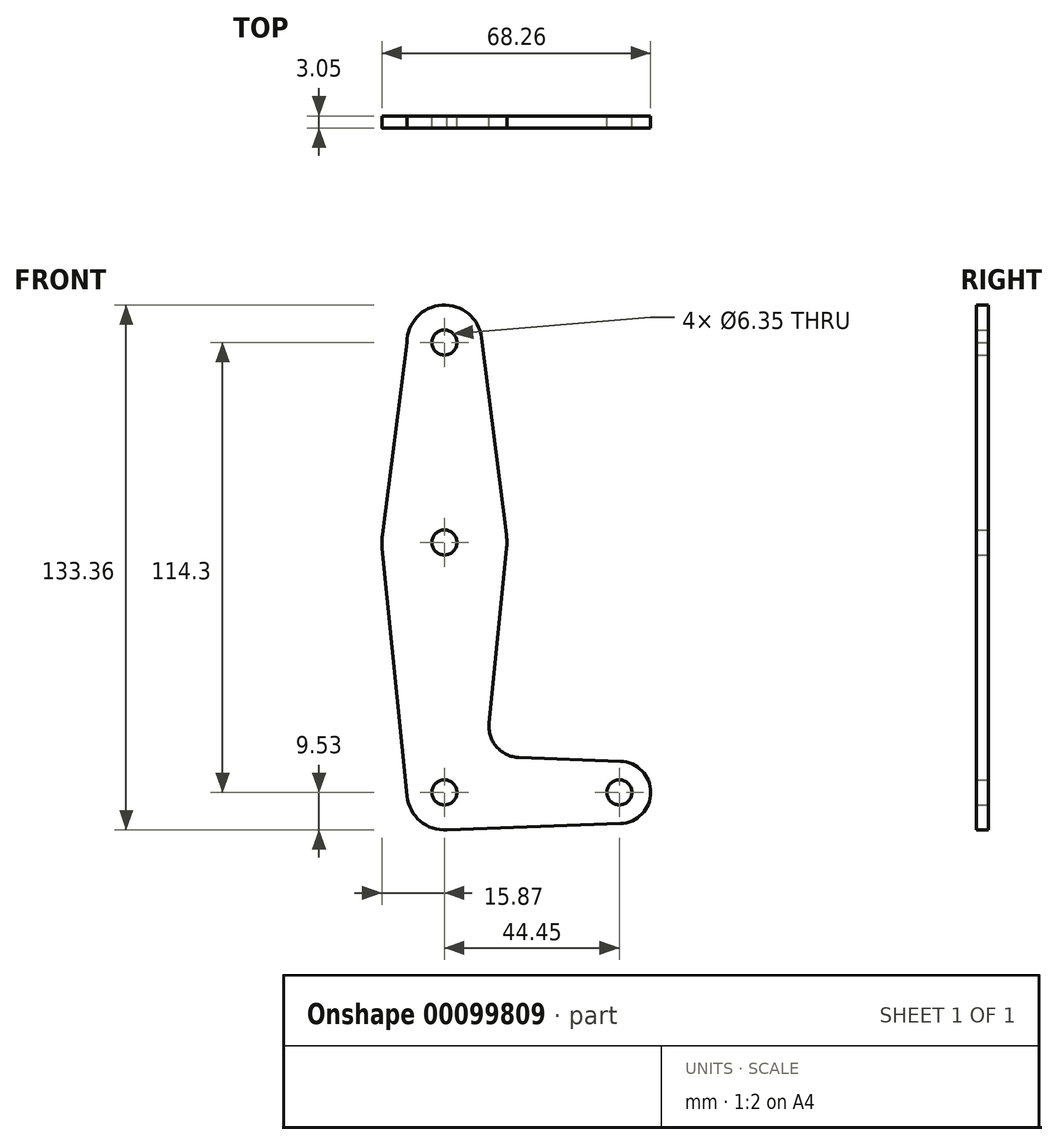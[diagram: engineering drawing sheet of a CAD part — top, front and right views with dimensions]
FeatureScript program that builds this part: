
annotation { "Feature Type Name" : "Feature", "Feature Type Description" : "" }
export const myFeature = defineFeature(function(context is Context, id is Id, definition is map)
    precondition{}
    {
        {
            var Q0;
            Q0=qCreatedBy(makeId("Front.planeOp"),FACE);
            var sketch = newSketch(context, id + "F0", { "sketchPlane" : qUnion([Q0])});
            skLineSegment(sketch, "E0", {"start": v(0, 0) * mm, "end": v(0, 114.3) * mm, "construction": true});
            skLineSegment(sketch, "E1", {"start": v(0, 0) * mm, "end": v(44.45, 0) * mm, "construction": true});
            skCircle(sketch, "E2", {"center": v(0, 114.3) * mm, "radius": 9.53 * mm});
            skCircle(sketch, "E3", {"center": v(0, 63.5) * mm, "radius": 15.88 * mm});
            skCircle(sketch, "E4", {"center": v(0, 0) * mm, "radius": 9.53 * mm});
            skCircle(sketch, "E5", {"center": v(44.45, 0) * mm, "radius": 7.94 * mm});
            skLineSegment(sketch, "E6", {"start": v(-9.53, 114.3) * mm, "end": v(-15.75, 65.5) * mm});
            skLineSegment(sketch, "E7", {"start": v(9.45, 115.5) * mm, "end": v(15.75, 65.48) * mm});
            skLineSegment(sketch, "E8", {"start": v(18.97, 8.85) * mm, "end": v(44.73, 7.93) * mm});
            skLineSegment(sketch, "E9", {"start": v(0, -9.53) * mm, "end": v(44.73, -7.93) * mm});
            skLineSegment(sketch, "E10", {"start": v(-15.8, 61.91) * mm, "end": v(-9.48, -0.95) * mm});
            skLineSegment(sketch, "E11", {"start": v(11.34, 17.6) * mm, "end": v(15.8, 61.91) * mm});
            skCircle(sketch, "E12", {"center": v(0, 114.3) * mm, "radius": 3.18 * mm});
            skCircle(sketch, "E13", {"center": v(0, 63.5) * mm, "radius": 3.18 * mm});
            skCircle(sketch, "E14", {"center": v(0, 0) * mm, "radius": 3.18 * mm});
            skCircle(sketch, "E15", {"center": v(44.45, 0) * mm, "radius": 3.18 * mm});
            skArc(sketch, "E16.filletArc", {"start": v(11.34, 17.6) * mm, "mid": v(13.26, 11.57) * mm, "end": v(18.97, 8.85) * mm});
            skSolve(sketch);
        }
        {
            var Q0;
            Q0 = qSketchRegion(id + "F0", true);
            extrude(context, id + "F1", {"entities" : qUnion([Q0]), "depth" : 3.05 * mm});
        }
    });
